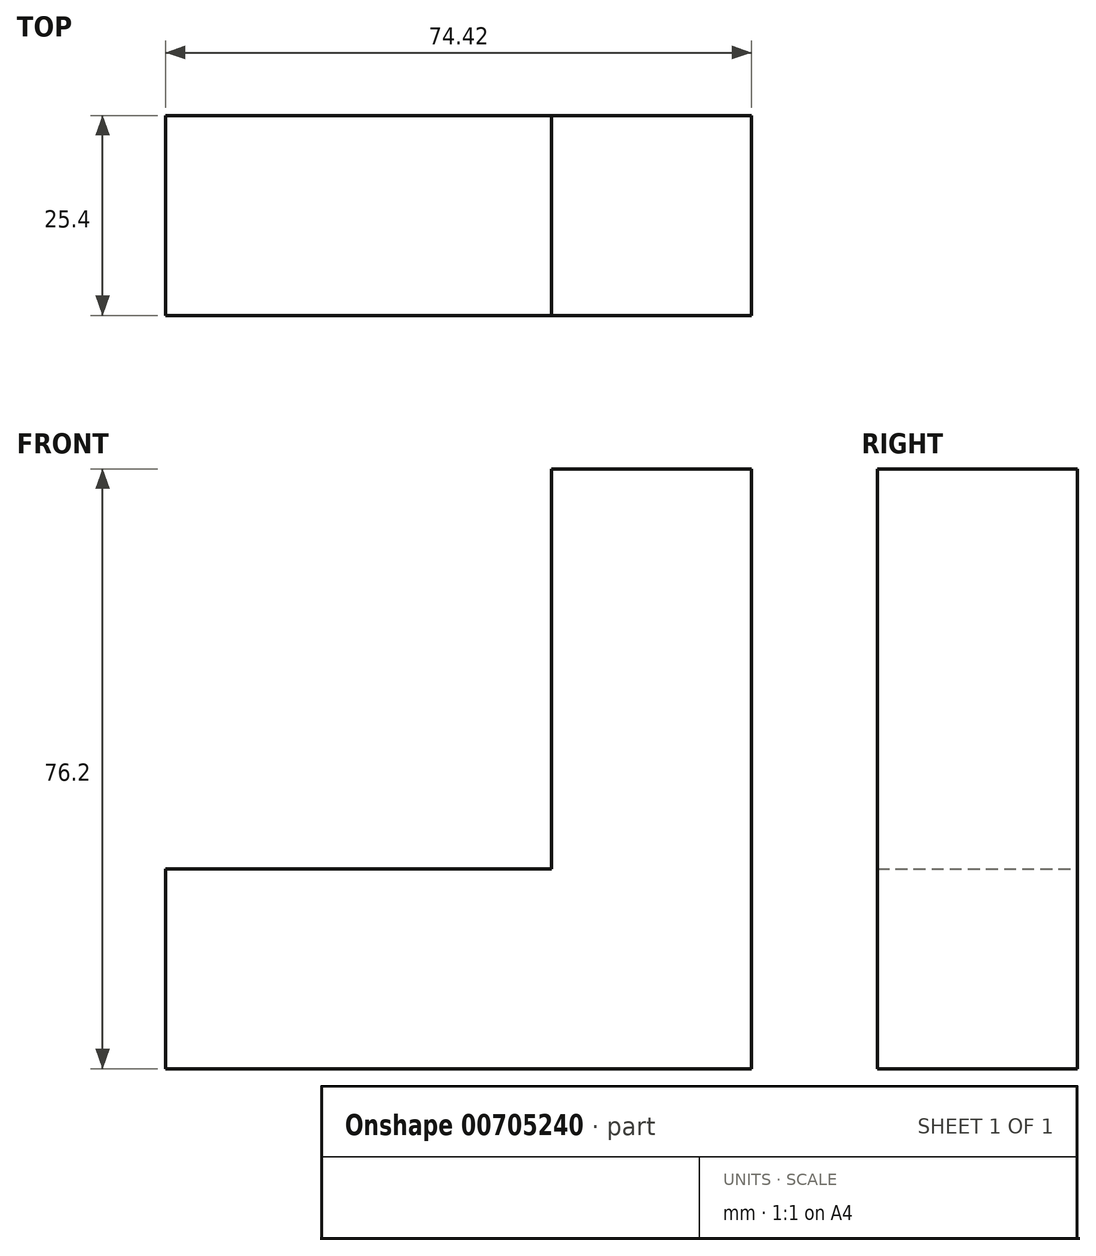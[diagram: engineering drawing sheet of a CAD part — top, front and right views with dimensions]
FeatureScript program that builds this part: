
annotation { "Feature Type Name" : "Feature", "Feature Type Description" : "" }
export const myFeature = defineFeature(function(context is Context, id is Id, definition is map)
    precondition{}
    {
        {
            var Q0;
            Q0=qCreatedBy(makeId("Front.planeOp"),FACE);
            var sketch = newSketch(context, id + "F0", { "sketchPlane" : qUnion([Q0])});
            skLineSegment(sketch, "E0.bottom", {"start": v(0, 25.4) * mm, "end": v(-25.4, 25.4) * mm});
            skLineSegment(sketch, "E0.top", {"start": v(0, 0) * mm, "end": v(-25.4, 0) * mm});
            skLineSegment(sketch, "E0.left", {"start": v(0, 25.4) * mm, "end": v(0, 0) * mm});
            skLineSegment(sketch, "E0.right", {"start": v(-25.4, 25.4) * mm, "end": v(-25.4, 0) * mm});
            skLineSegment(sketch, "E1.bottom", {"start": v(-25.4, 25.4) * mm, "end": v(-49.02, 25.4) * mm});
            skLineSegment(sketch, "E1.top", {"start": v(-25.4, 0) * mm, "end": v(-49.02, 0) * mm});
            skLineSegment(sketch, "E1.right", {"start": v(-49.02, 25.4) * mm, "end": v(-49.02, 0) * mm});
            skLineSegment(sketch, "E2.bottom", {"start": v(0, 25.4) * mm, "end": v(25.4, 25.4) * mm});
            skLineSegment(sketch, "E2.top", {"start": v(0, 0) * mm, "end": v(25.4, 0) * mm});
            skLineSegment(sketch, "E2.right", {"start": v(25.4, 25.4) * mm, "end": v(25.4, 0) * mm});
            skLineSegment(sketch, "E3.bottom", {"start": v(-25.4, 25.4) * mm, "end": v(0, 25.4) * mm});
            skLineSegment(sketch, "E3.top", {"start": v(-25.4, 50.8) * mm, "end": v(0, 50.8) * mm});
            skLineSegment(sketch, "E3.left", {"start": v(-25.4, 25.4) * mm, "end": v(-25.4, 50.8) * mm});
            skLineSegment(sketch, "E3.right", {"start": v(0, 25.4) * mm, "end": v(0, 50.8) * mm});
            skLineSegment(sketch, "E4.bottom", {"start": v(0, 50.8) * mm, "end": v(25.4, 50.8) * mm});
            skLineSegment(sketch, "E4.left", {"start": v(0, 50.8) * mm, "end": v(0, 25.4) * mm});
            skLineSegment(sketch, "E4.right", {"start": v(25.4, 50.8) * mm, "end": v(25.4, 25.4) * mm});
            skLineSegment(sketch, "E5.top", {"start": v(0, 76.2) * mm, "end": v(25.4, 76.2) * mm});
            skLineSegment(sketch, "E5.left", {"start": v(0, 50.8) * mm, "end": v(0, 76.2) * mm});
            skLineSegment(sketch, "E5.right", {"start": v(25.4, 50.8) * mm, "end": v(25.4, 76.2) * mm});
            skSolve(sketch);
        }
        {
            var Q0;
            Q0=makeQuery(id+"F0.imprint","IMPRINT",FACE,{"disambiguationData":[TD([[makeQuery(id+"F0.imprint","IMPRINT",EDGE,{"derivedFrom":sQuery(id+"F0.wireOp",EDGE,"E4.bottom")}),1.0]])]});
            var Q1;
            Q1=makeQuery(id+"F0.imprint","IMPRINT",FACE,{"disambiguationData":[TD([[makeQuery(id+"F0.imprint","IMPRINT",EDGE,{"derivedFrom":sQuery(id+"F0.wireOp",EDGE,"E3.bottom")}),1.0]])]});
            var Q2;
            Q2=makeQuery(id+"F0.imprint","IMPRINT",FACE,{"disambiguationData":[TD([[makeQuery(id+"F0.imprint","IMPRINT",EDGE,{"derivedFrom":sQuery(id+"F0.wireOp",EDGE,"E2.bottom")}),1.0]])]});
            var Q3;
            Q3=makeQuery(id+"F0.imprint","IMPRINT",FACE,{"disambiguationData":[TD([[makeQuery(id+"F0.imprint","IMPRINT",EDGE,{"derivedFrom":sQuery(id+"F0.wireOp",EDGE,"E2.top")}),1.0]])]});
            var Q4;
            Q4=makeQuery(id+"F0.imprint","IMPRINT",FACE,{"disambiguationData":[TD([[makeQuery(id+"F0.imprint","IMPRINT",EDGE,{"derivedFrom":sQuery(id+"F0.wireOp",EDGE,"E0.top")}),-1.0]])]});
            var Q5;
            Q5=makeQuery(id+"F0.imprint","IMPRINT",FACE,{"disambiguationData":[TD([[makeQuery(id+"F0.imprint","IMPRINT",EDGE,{"derivedFrom":sQuery(id+"F0.wireOp",EDGE,"E1.bottom")}),1.0]])]});
            extrude(context, id + "F1", {"entities" : qUnion([Q0, Q1, Q2, Q3, Q4, Q5]), "depth" : 25.4 * mm, "offsetDistance" : 25.4 * mm});
        }
    });
